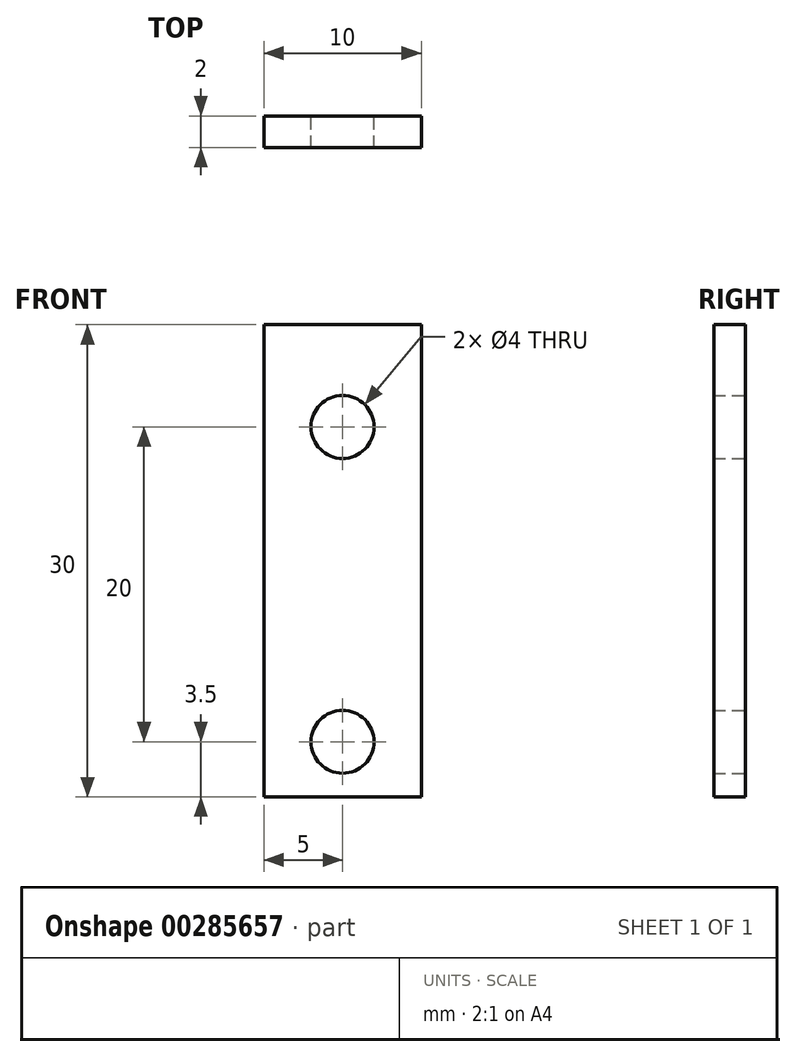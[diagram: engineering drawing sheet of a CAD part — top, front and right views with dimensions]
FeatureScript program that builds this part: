
annotation { "Feature Type Name" : "Feature", "Feature Type Description" : "" }
export const myFeature = defineFeature(function(context is Context, id is Id, definition is map)
    precondition{}
    {
        {
            var Q0;
            Q0=qCreatedBy(makeId("Front.planeOp"),FACE);
            var sketch = newSketch(context, id + "F0", { "sketchPlane" : qUnion([Q0])});
            skLineSegment(sketch, "E0.bottom", {"start": v(5, -15) * mm, "end": v(-5, -15) * mm});
            skLineSegment(sketch, "E0.top", {"start": v(5, 15) * mm, "end": v(-5, 15) * mm});
            skLineSegment(sketch, "E0.left", {"start": v(5, -15) * mm, "end": v(5, 15) * mm});
            skLineSegment(sketch, "E0.right", {"start": v(-5, -15) * mm, "end": v(-5, 15) * mm});
            skPoint(sketch, "E0.middle", {"position": v(0, 0) * mm});
            skCircle(sketch, "E1", {"center": v(0, 8.5) * mm, "radius": 2 * mm});
            skCircle(sketch, "E2", {"center": v(0, -11.5) * mm, "radius": 2 * mm});
            skSolve(sketch);
        }
        {
            var Q0;
            Q0=makeQuery(id+"F0.imprint","IMPRINT",FACE,{"disambiguationData":[TD([[makeQuery(id+"F0.imprint","IMPRINT",EDGE,{"derivedFrom":sQuery(id+"F0.wireOp",EDGE,"E0.bottom")}),-1.0]])]});
            extrude(context, id + "F1", {"entities" : qUnion([Q0]), "depth" : 2 * mm, "offsetDistance" : 25 * mm});
        }
    });
